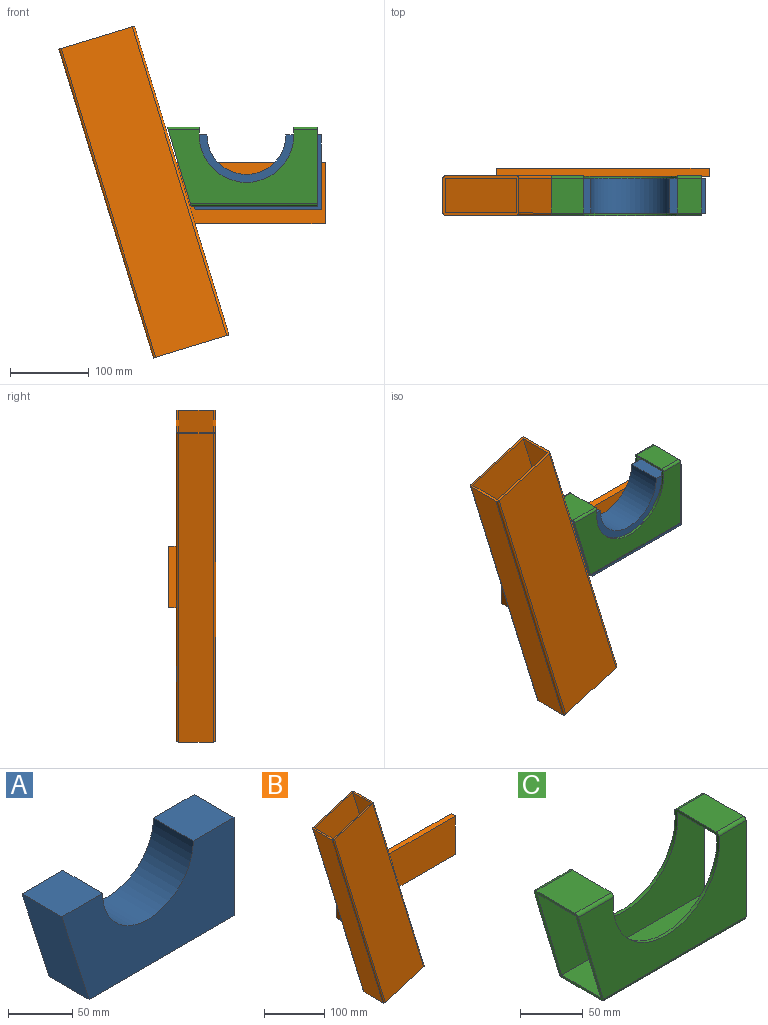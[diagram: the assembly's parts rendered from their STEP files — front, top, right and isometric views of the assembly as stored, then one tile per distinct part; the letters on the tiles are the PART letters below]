
ASSEMBLY  parts=3 mates=3
PART A: 8 faces, bbox 190x44x94 mm
  f0: plane 160x44mm, normal (0,0,-1), area 7040mm2, adj f1,f2,f5,f7
  f1: plane 190x94mm, normal (0,-1,0), area 12523mm2, adj f0,f3,f4,f5,f6,f7
  f2: plane 190x94mm, normal (0,1,0), area 12523mm2, adj f0,f3,f4,f5,f6,f7
  f3: cylinder r=50mm len=100mm, axis (0,1,0), area 6911.5mm2, adj f1,f2,f4,f6
  f4: plane 45x44mm, normal (0,0,1), area 1980mm2, adj f1,f2,f3,f7
  f5: plane 94x44mm, normal (1,0,0), area 4136mm2, adj f0,f1,f2,f6
  f6: plane 45x44mm, normal (0,0,1), area 1980mm2, adj f1,f2,f3,f5
  f7: plane 94x44mm, normal (-0.95,0,-0.3), area 4341.5mm2, adj f0,f1,f2,f4
PART B: 22 faces, bbox 336.9x60x420.3 mm
  f0: plane 239.23x142.32mm, normal (0,1,0), area 16207.5mm2, adj f4,f6,f14,f17,f18
  f1: plane 418.55x209.46mm, normal (0,-1,0), area 38440.4mm2, adj f2,f12,f13,f14
  f2: cylinder r=3mm len=391.95mm, axis (-0.29,0,0.96), area 1927.1mm2, adj f1,f3,f13,f14
  f3: plane 391.07x119.56mm, normal (-0.96,0,-0.29), area 17993.4mm2, adj f2,f4,f13,f14
  f4: cylinder r=3mm len=391.95mm, axis (-0.29,0,0.96), area 1927.1mm2, adj f0,f3,f5,f13,f14,f15
  f5: plane 169.06x141.58mm, normal (0,1,0), area 15267.3mm2, adj f4,f6,f13,f16
  f6: cylinder r=3mm len=391.95mm, axis (-0.29,0,0.96), area 1927.1mm2, adj f0,f5,f7,f13,f14,f21
  f7: plane 391.07x119.56mm, normal (0.96,0,0.29), area 17993.4mm2, adj f6,f12,f13,f14
  f8: plane 391.07x119.56mm, normal (-0.96,0,-0.29), area 17993.4mm2, adj f9,f11,f13,f14
  f9: plane 418.55x209.46mm, normal (0,-1,0), area 38440.4mm2, adj f8,f10,f13,f14
  f10: plane 391.07x119.56mm, normal (0.96,0,0.29), area 17993.4mm2, adj f9,f11,f13,f14
  f11: plane 418.55x209.46mm, normal (0,1,0), area 38440.4mm2, adj f8,f10,f13,f14
  f12: cylinder r=3mm len=391.95mm, axis (-0.29,0,0.96), area 1927.1mm2, adj f1,f7,f13,f14
  f13: plane 95.63x50mm, normal (0.29,0,-0.96), area 856.3mm2, adj f1,f2,f3,f4,f5,f6,f7,f8
  f14: plane 95.63x50mm, normal (-0.29,0,0.96), area 856.3mm2, adj f0,f1,f2,f3,f4,f6,f7,f8
  f15: plane 10.26x3.14mm, normal (0,-1,0), area 16.1mm2, adj f4,f16,f17
  f16: plane 269.3x10mm, normal (0,0,-1), area 2693mm2, adj f5,f15,f17,f19,f20,f21
  f17: plane 78x10mm, normal (-1,0,0), area 780mm2, adj f0,f15,f16,f18,f20
  f18: plane 269.3x10mm, normal (0,0,1), area 2693mm2, adj f0,f17,f19,f20,f21
  f19: plane 78x10mm, normal (1,0,0), area 780mm2, adj f16,f18,f20,f21
  f20: plane 269.3x78mm, normal (0,1,0), area 21005.6mm2, adj f16,f17,f18,f19
  f21: plane 191.72x78mm, normal (0,-1,0), area 14024mm2, adj f6,f16,f18,f19
PART C: 19 faces, bbox 190x50x100 mm
  f0: plane 44x40.84mm, normal (0,0,1), area 1796.9mm2, adj f3,f5,f17,f18
  f1: plane 44x30.41mm, normal (0,0,-1), area 1338mm2, adj f7,f15,f16,f18
  f2: plane 44x39.51mm, normal (0,0,-1), area 1738.4mm2, adj f7,f15,f17,f18
  f3: cylinder r=3mm len=40.84mm, axis (-1,0,0), area 190.1mm2, adj f0,f12,f17,f18
  f4: cylinder r=3mm len=30.84mm, axis (-1,0,0), area 144.5mm2, adj f12,f13,f16,f18
  f5: cylinder r=3mm len=40.84mm, axis (-1,0,0), area 190.1mm2, adj f0,f14,f17,f18
  f6: cylinder r=3mm len=30.84mm, axis (-1,0,0), area 144.5mm2, adj f13,f14,f16,f18
  f7: plane 189.1x94mm, normal (0,-1,0), area 9957mm2, adj f1,f2,f8,f16,f17,f18
  f8: plane 160.9x44mm, normal (0,0,1), area 7079.6mm2, adj f7,f15,f16,f17
  f9: cylinder r=3mm len=160.9mm, axis (-1,0,0), area 755.5mm2, adj f10,f14,f16,f17
  f10: plane 160x44mm, normal (0,0,-1), area 7040mm2, adj f9,f11,f16,f17
  f11: cylinder r=3mm len=160.9mm, axis (-1,0,0), area 755.5mm2, adj f10,f12,f16,f17
  f12: plane 189.1x94mm, normal (0,1,0), area 9957mm2, adj f3,f4,f11,f16,f17,f18
  f13: plane 44x30.84mm, normal (0,0,1), area 1356.9mm2, adj f4,f6,f16,f18
  f14: plane 189.1x94mm, normal (0,-1,0), area 9957mm2, adj f5,f6,f9,f16,f17,f18
  f15: plane 189.1x94mm, normal (0,1,0), area 9957mm2, adj f1,f2,f8,f16,f17,f18
  f16: plane 100x50mm, normal (1,0,0), area 856.3mm2, adj f1,f4,f6,f7,f8,f9,f10,f11
  f17: plane 100x50mm, normal (-0.96,0,-0.29), area 894mm2, adj f0,f2,f3,f5,f7,f8,f9,f10
  f18: cylinder r=60mm len=120mm, axis (0,1,0), area 1510.4mm2, adj f0,f1,f2,f3,f4,f5,f6,f7
PLACE A t=(104.46,410.77,26.97)mm
PLACE B t=(-24.94,388.77,47.55)mm
PLACE C t=(4.46,388.77,80.97)mm
MATE planar B.f21 <-> C.f12  axis (0,-1,0) through (113.97,413.77,48.42)mm
MATE planar A.f1 <-> C.f15  axis (0,-1,0) through (114.03,366.77,67.65)mm
MATE cylindrical A.f3 <-> C.f18  axis (0,1,0) through (104.46,366.77,120.97)mm
